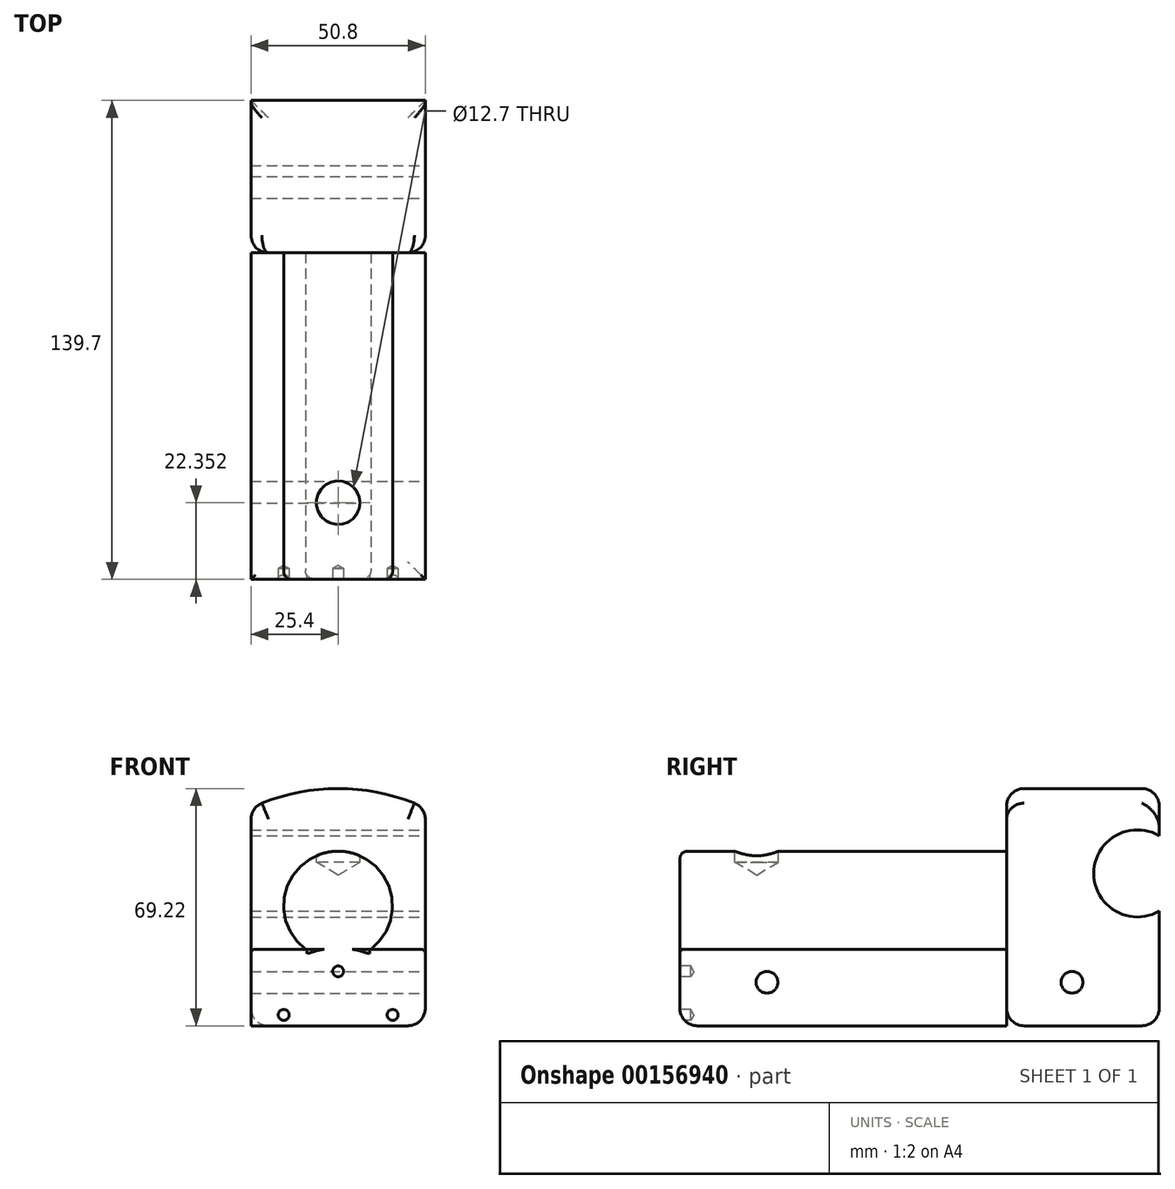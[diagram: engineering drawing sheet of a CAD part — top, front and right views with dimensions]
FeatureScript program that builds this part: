
annotation { "Feature Type Name" : "Feature", "Feature Type Description" : "" }
export const myFeature = defineFeature(function(context is Context, id is Id, definition is map)
    precondition{}
    {
        {
            var Q0;
            Q0=qCreatedBy(makeId("Front.planeOp"),FACE);
            var sketch = newSketch(context, id + "F0", { "sketchPlane" : qUnion([Q0])});
            skLineSegment(sketch, "E0.bottom", {"start": v(25.4, -11.18) * mm, "end": v(-25.4, -11.18) * mm});
            skLineSegment(sketch, "E0.top", {"start": v(25.4, 11.18) * mm, "end": v(-25.4, 11.18) * mm});
            skLineSegment(sketch, "E0.left", {"start": v(25.4, -11.18) * mm, "end": v(25.4, 11.18) * mm});
            skLineSegment(sketch, "E0.right", {"start": v(-25.4, -11.18) * mm, "end": v(-25.4, 11.18) * mm});
            skPoint(sketch, "E0.middle", {"position": v(0, 0) * mm});
            skCircle(sketch, "E1", {"center": v(0, 23.88) * mm, "radius": 15.88 * mm});
            skLineSegment(sketch, "E2.bottom", {"start": v(-25.4, -11.18) * mm, "end": v(-15.88, -11.18) * mm});
            skLineSegment(sketch, "E2.left", {"start": v(-25.4, -11.18) * mm, "end": v(-25.4, -8) * mm});
            skPoint(sketch, "E3", {"position": v(-15.88, -8) * mm});
            skLineSegment(sketch, "E4", {"start": v(0, 0) * mm, "end": v(0, -11.18) * mm});
            skPoint(sketch, "E5", {"position": v(15.88, -8) * mm});
            skPoint(sketch, "E6.MirrorCS.start.orphan", {"position": v(25.4, -8) * mm});
            skLineSegment(sketch, "E7.bottom", {"start": v(-25.4, -11.18) * mm, "end": v(0, -11.18) * mm});
            skLineSegment(sketch, "E7.top", {"start": v(-25.4, 4.7) * mm, "end": v(0, 4.7) * mm});
            skLineSegment(sketch, "E7.left", {"start": v(-25.4, -11.18) * mm, "end": v(-25.4, 4.7) * mm});
            skLineSegment(sketch, "E7.right", {"start": v(0, -11.18) * mm, "end": v(0, 4.7) * mm});
            skPoint(sketch, "E8", {"position": v(0, 4.7) * mm});
            skSolve(sketch);
        }
        {
            var Q0;
            Q0 = qSketchRegion(id + "F0", true);
            extrude(context, id + "F1", {"entities" : qUnion([Q0]), "oppositeDirection" : true, "depth" : 95.25 * mm});
        }
        {
            var Q0;
            Q0=sQuery(id+"F0.wireOp",VERTEX,"E8");
            var Q1;
            Q1=sQuery(id+"F0.wireOp",VERTEX,"E5");
            var Q2;
            Q2=sQuery(id+"F0.wireOp",VERTEX,"E3");
            var Q3;
            Q3=makeQuery(id+"F1.opExtrude","SWEPT_BODY",BODY,{"disambiguationData":[OSD([sQuery(id+"F0.wireOp",EDGE,"E0.bottom"),sQuery(id+"F0.wireOp",EDGE,"E0.top"),sQuery(id+"F0.wireOp",EDGE,"E0.left"),sQuery(id+"F0.wireOp",EDGE,"E0.right"),sQuery(id+"F0.wireOp",EDGE,"E1"),sQuery(id+"F0.wireOp",EDGE,"E7.bottom"),sQuery(id+"F0.wireOp",EDGE,"E7.left")])]});
            hole(context, id + "F2", {"style" : HoleStyle.SIMPLE, "endStyle" : HoleEndStyle.BLIND, "holeDiameter" : 3.17 * mm, "holeDepth" : 3.17 * mm, "startFromSketch" : true, "locations" : qUnion([Q0, Q1, Q2]), "scope" : qUnion([Q3])});
        }
        {
            var Q0;
            Q0=makeQuery(id+"F1.opExtrude","SWEPT_FACE",FACE,{"disambiguationData":[OSD([sQuery(id+"F0.wireOp",EDGE,"E0.bottom"),sQuery(id+"F0.wireOp",EDGE,"E7.bottom")])]});
            cPlane(context, id + "F3", {"entities" : qUnion([Q0]), "cplaneType" : CPlaneType.OFFSET, "offset" : 54.1 * mm, "oppositeDirection" : true, "width" : 152.4 * mm, "height" : 152.4 * mm});
        }
        {
            var Q0;
            Q0=qCreatedBy(id+"F3.planeOp",FACE);
            var sketch = newSketch(context, id + "F4", { "sketchPlane" : qUnion([Q0])});
            skLineSegment(sketch, "E9.0", {"start": v(-15.88, 0) * mm, "end": v(15.88, 0) * mm});
            skLineSegment(sketch, "E10", {"start": v(0, 0) * mm, "end": v(0, -22.35) * mm});
            skPoint(sketch, "E11", {"position": v(0, -22.35) * mm});
            skSolve(sketch);
        }
        {
            var Q0;
            Q0=sQuery(id+"F4.wireOp",VERTEX,"E11");
            var Q1;
            Q1=makeQuery(id+"F1.opExtrude","SWEPT_BODY",BODY,{"disambiguationData":[OSD([sQuery(id+"F0.wireOp",EDGE,"E0.bottom"),sQuery(id+"F0.wireOp",EDGE,"E0.top"),sQuery(id+"F0.wireOp",EDGE,"E0.left"),sQuery(id+"F0.wireOp",EDGE,"E0.right"),sQuery(id+"F0.wireOp",EDGE,"E1"),sQuery(id+"F0.wireOp",EDGE,"E7.bottom"),sQuery(id+"F0.wireOp",EDGE,"E7.left")])]});
            hole(context, id + "F5", {"style" : HoleStyle.SIMPLE, "endStyle" : HoleEndStyle.BLIND, "oppositeDirection" : true, "holeDiameter" : 12.7 * mm, "holeDepth" : 6.35 * mm, "startFromSketch" : true, "locations" : qUnion([Q0]), "scope" : qUnion([Q1])});
        }
        {
            var Q0;
            Q0=makeQuery(id+"F1.opExtrude","CAP_FACE",FACE,{"disambiguationData":[OSD([sQuery(id+"F0.wireOp",EDGE,"E0.bottom"),sQuery(id+"F0.wireOp",EDGE,"E0.top"),sQuery(id+"F0.wireOp",EDGE,"E0.left"),sQuery(id+"F0.wireOp",EDGE,"E0.right"),sQuery(id+"F0.wireOp",EDGE,"E1"),sQuery(id+"F0.wireOp",EDGE,"E7.bottom"),sQuery(id+"F0.wireOp",EDGE,"E7.left")])],"isStart":false});
            var sketch = newSketch(context, id + "F6", { "sketchPlane" : qUnion([Q0])});
            skLineSegment(sketch, "E12", {"start": v(-25.4, -11.18) * mm, "end": v(-25.4, -1.65) * mm});
            skLineSegment(sketch, "E13", {"start": v(-25.4, -1.65) * mm, "end": v(0, -1.65) * mm});
            skPoint(sketch, "E14", {"position": v(0, -1.65) * mm});
            skArc(sketch, "E15", {"start": v(25.4, 52.37) * mm, "mid": v(0, 58.04) * mm, "end": v(-25.4, 52.37) * mm});
            skLineSegment(sketch, "E16", {"start": v(-25.4, 11.18) * mm, "end": v(-25.4, 52.37) * mm});
            skLineSegment(sketch, "E17", {"start": v(25.4, 11.18) * mm, "end": v(25.4, 52.37) * mm});
            skSolve(sketch);
        }
        {
            var Q0;
            Q0 = qSketchRegion(id + "F6", true);
            var Q1;
            Q1=makeQuery(id+"F6.imprint","IMPRINT",FACE,{"disambiguationData":[TD([[makeQuery(id+"F6.imprint","IMPRINT",EDGE,{"derivedFrom":sQuery(id+"F6.wireOp",EDGE,"E15")}),1.0]])]});
            var Q2;
            {var subQ5=sQuery(id+"F6.wireOp",EDGE,"E12");Q2=makeQuery(id+"F6.imprint","IMPRINT",FACE,{"disambiguationData":[TD([[makeQuery(id+"F6.imprint","IMPRINT",EDGE,{"derivedFrom":subQ5}),-1.0]])]});}
            extrude(context, id + "F7", {"entities" : qUnion([Q0, Q1, Q2]), "depth" : 44.45 * mm});
        }
        {
            var Q0;
            Q0=makeQuery(id+"F7.opExtrude","SWEPT_FACE",FACE,{"disambiguationData":[OSD([sQuery(id+"F0.wireOp",EDGE,"E0.left"),sQuery(id+"F6.wireOp",EDGE,"E12"),sQuery(id+"F6.wireOp",EDGE,"E16")])]});
            var sketch = newSketch(context, id + "F8", { "sketchPlane" : qUnion([Q0])});
            skLineSegment(sketch, "E18.bottom", {"start": v(139.7, -11.18) * mm, "end": v(133.35, -11.18) * mm});
            skLineSegment(sketch, "E18.top", {"start": v(139.7, 33.27) * mm, "end": v(133.35, 33.27) * mm});
            skLineSegment(sketch, "E18.left", {"start": v(139.7, -11.18) * mm, "end": v(139.7, 33.27) * mm});
            skLineSegment(sketch, "E18.right", {"start": v(133.35, -11.18) * mm, "end": v(133.35, 33.27) * mm});
            skPoint(sketch, "E19", {"position": v(133.35, 33.27) * mm});
            skLineSegment(sketch, "E20.bottom", {"start": v(139.7, -11.18) * mm, "end": v(114.3, -11.18) * mm});
            skLineSegment(sketch, "E20.top", {"start": v(139.7, 1.52) * mm, "end": v(114.3, 1.52) * mm});
            skLineSegment(sketch, "E20.left", {"start": v(139.7, -11.18) * mm, "end": v(139.7, 1.52) * mm});
            skLineSegment(sketch, "E20.right", {"start": v(114.3, -11.18) * mm, "end": v(114.3, 1.52) * mm});
            skPoint(sketch, "E21", {"position": v(114.3, 1.52) * mm});
            skLineSegment(sketch, "E22.bottom", {"start": v(139.7, -11.18) * mm, "end": v(25.4, -11.18) * mm});
            skLineSegment(sketch, "E22.top", {"start": v(139.7, 1.52) * mm, "end": v(25.4, 1.52) * mm});
            skLineSegment(sketch, "E22.right", {"start": v(25.4, -11.18) * mm, "end": v(25.4, 1.52) * mm});
            skPoint(sketch, "E23", {"position": v(25.4, 1.52) * mm});
            skSolve(sketch);
        }
        {
            var Q0;
            Q0=sQuery(id+"F8.wireOp",VERTEX,"E23");
            var Q1;
            Q1=sQuery(id+"F8.wireOp",VERTEX,"E21");
            var Q2;
            Q2=makeQuery(id+"F7.opExtrude","SWEPT_BODY",BODY,{"disambiguationData":[OSD([sQuery(id+"F0.wireOp",EDGE,"E0.bottom"),sQuery(id+"F0.wireOp",EDGE,"E0.left"),sQuery(id+"F0.wireOp",EDGE,"E0.right"),sQuery(id+"F0.wireOp",EDGE,"E7.bottom"),sQuery(id+"F0.wireOp",EDGE,"E7.left"),sQuery(id+"F6.wireOp",EDGE,"E12"),sQuery(id+"F6.wireOp",EDGE,"E15"),sQuery(id+"F6.wireOp",EDGE,"E16"),sQuery(id+"F6.wireOp",EDGE,"E17")])]});
            var Q3;
            Q3=makeQuery(id+"F1.opExtrude","SWEPT_BODY",BODY,{"disambiguationData":[OSD([sQuery(id+"F0.wireOp",EDGE,"E0.bottom"),sQuery(id+"F0.wireOp",EDGE,"E0.top"),sQuery(id+"F0.wireOp",EDGE,"E0.left"),sQuery(id+"F0.wireOp",EDGE,"E0.right"),sQuery(id+"F0.wireOp",EDGE,"E1"),sQuery(id+"F0.wireOp",EDGE,"E7.bottom"),sQuery(id+"F0.wireOp",EDGE,"E7.left")])]});
            hole(context, id + "F9", {"style" : HoleStyle.SIMPLE, "endStyle" : HoleEndStyle.THROUGH, "holeDiameter" : 6.35 * mm, "startFromSketch" : true, "locations" : qUnion([Q0, Q1]), "scope" : qUnion([Q2, Q3]), "isTappedThrough" : true});
        }
        {
            var Q0;
            Q0=sQuery(id+"F8.wireOp",VERTEX,"E19");
            var Q1;
            Q1=makeQuery(id+"F7.opExtrude","SWEPT_BODY",BODY,{"disambiguationData":[OSD([sQuery(id+"F0.wireOp",EDGE,"E0.bottom"),sQuery(id+"F0.wireOp",EDGE,"E0.left"),sQuery(id+"F0.wireOp",EDGE,"E0.right"),sQuery(id+"F0.wireOp",EDGE,"E7.bottom"),sQuery(id+"F0.wireOp",EDGE,"E7.left"),sQuery(id+"F6.wireOp",EDGE,"E12"),sQuery(id+"F6.wireOp",EDGE,"E15"),sQuery(id+"F6.wireOp",EDGE,"E16"),sQuery(id+"F6.wireOp",EDGE,"E17")])]});
            hole(context, id + "F10", {"style" : HoleStyle.SIMPLE, "endStyle" : HoleEndStyle.THROUGH, "holeDiameter" : 25.4 * mm, "startFromSketch" : true, "locations" : qUnion([Q0]), "scope" : qUnion([Q1]), "isTappedThrough" : true});
        }
        {
            var Q0;
            Q0=makeQuery(id+"F7.opExtrude","CAP_EDGE",EDGE,{"disambiguationData":[OSD([sQuery(id+"F6.wireOp",EDGE,"E15")])],"isStart":true});
            var Q1;
            Q1=makeQuery(id+"F7.opExtrude","SWEPT_EDGE",EDGE,{"disambiguationData":[OSD([sQuery(id+"F6.wireOp",EDGE,"E15"),sQuery(id+"F6.wireOp",EDGE,"E17")])]});
            var Q2;
            Q2=makeQuery(id+"F7.opExtrude","CAP_EDGE",EDGE,{"disambiguationData":[OSD([sQuery(id+"F6.wireOp",EDGE,"E15")])],"isStart":false});
            var Q3;
            Q3=makeQuery(id+"F7.opExtrude","SWEPT_EDGE",EDGE,{"disambiguationData":[OSD([sQuery(id+"F6.wireOp",EDGE,"E15"),sQuery(id+"F6.wireOp",EDGE,"E16")])]});
            var Q4;
            Q4=makeQuery(id+"F7.opExtrude","CAP_EDGE",EDGE,{"disambiguationData":[OSD([sQuery(id+"F0.wireOp",EDGE,"E0.bottom"),sQuery(id+"F0.wireOp",EDGE,"E7.bottom")])],"isStart":false});
            var Q5;
            Q5=makeQuery(id+"F7.opExtrude","SWEPT_EDGE",EDGE,{"disambiguationData":[OSD([sQuery(id+"F0.wireOp",EDGE,"E0.bottom"),sQuery(id+"F0.wireOp",EDGE,"E7.bottom"),sQuery(id+"F6.wireOp",EDGE,"E12")])]});
            var Q6;
            Q6=makeQuery(id+"F1.opExtrude","SWEPT_EDGE",EDGE,{"disambiguationData":[OSD([sQuery(id+"F0.wireOp",EDGE,"E0.bottom"),sQuery(id+"F0.wireOp",EDGE,"E0.left")])]});
            var Q7;
            Q7=makeQuery(id+"F7.opExtrude","SWEPT_EDGE",EDGE,{"disambiguationData":[OSD([sQuery(id+"F0.wireOp",EDGE,"E0.bottom"),sQuery(id+"F0.wireOp",EDGE,"E0.right"),sQuery(id+"F0.wireOp",EDGE,"E7.bottom"),sQuery(id+"F0.wireOp",EDGE,"E7.left")])]});
            var Q8;
            Q8=makeQuery(id+"F1.opExtrude","SWEPT_EDGE",EDGE,{"disambiguationData":[OSD([sQuery(id+"F0.wireOp",EDGE,"E7.bottom"),sQuery(id+"F0.wireOp",EDGE,"E7.left")])]});
            var Q9;
            Q9=makeQuery(id+"F1.opExtrude","CAP_EDGE",EDGE,{"disambiguationData":[OSD([sQuery(id+"F0.wireOp",EDGE,"E0.bottom"),sQuery(id+"F0.wireOp",EDGE,"E7.bottom")])],"isStart":true});
            fillet(context, id + "F11", {"entities" : qUnion([Q0, Q1, Q2, Q3, Q4, Q5, Q6, Q7, Q8, Q9]), "radius" : 5.08 * mm, "tangentPropagation" : true, "allowEdgeOverflow" : false});
        }
        {
            var Q0;
            Q0=makeQuery(id+"F1.opExtrude","CAP_EDGE",EDGE,{"disambiguationData":[OSD([sQuery(id+"F0.wireOp",EDGE,"E1")])],"isStart":true});
            fillet(context, id + "F12", {"entities" : qUnion([Q0]), "radius" : 2.54 * mm, "rho" : 0.5, "crossSection" : FilletCrossSection.CONIC, "allowEdgeOverflow" : false});
        }
        {
            var Q0;
            Q0=makeQuery(id+"F1.opExtrude","SWEPT_EDGE",EDGE,{"disambiguationData":[OSD([sQuery(id+"F0.wireOp",EDGE,"E0.top"),sQuery(id+"F0.wireOp",EDGE,"E0.left")])]});
            var Q1;
            {var subQ0=sQuery(id+"F0.wireOp",EDGE,"E0.top");Q1=makeQuery(id+"F1.opExtrude","CAP_EDGE",EDGE,{"disambiguationData":[OSD([subQ0]),TDD([makeQuery(id+"F0.imprint","IMPRINT",EDGE,{"disambiguationData":[TD([[makeQuery(id+"F0.imprint","INTERSECT",VERTEX,{"derivedFrom":[subQ0,sQuery(id+"F0.wireOp",EDGE,"E0.left")]}),-1.0]])],"derivedFrom":subQ0})])],"isStart":true});}
            var Q2;
            {var subQ0=sQuery(id+"F0.wireOp",EDGE,"E0.top");Q2=makeQuery(id+"F1.opExtrude","CAP_EDGE",EDGE,{"disambiguationData":[OSD([subQ0]),TDD([makeQuery(id+"F0.imprint","IMPRINT",EDGE,{"disambiguationData":[TD([[makeQuery(id+"F0.imprint","INTERSECT",VERTEX,{"derivedFrom":[subQ0,sQuery(id+"F0.wireOp",EDGE,"E0.right")]}),1.0]])],"derivedFrom":subQ0})])],"isStart":true});}
            var Q3;
            Q3=makeQuery(id+"F1.opExtrude","SWEPT_EDGE",EDGE,{"disambiguationData":[OSD([sQuery(id+"F0.wireOp",EDGE,"E0.top"),sQuery(id+"F0.wireOp",EDGE,"E0.right")])]});
            fillet(context, id + "F13", {"entities" : qUnion([Q0, Q1, Q2, Q3]), "radius" : 1.27 * mm, "tangentPropagation" : true, "allowEdgeOverflow" : false});
        }
        {
            var Q0;
            Q0=makeQuery(id+"F7.opExtrude","CAP_EDGE",EDGE,{"disambiguationData":[OSD([sQuery(id+"F0.wireOp",EDGE,"E0.right"),sQuery(id+"F0.wireOp",EDGE,"E7.left"),sQuery(id+"F6.wireOp",EDGE,"E17")])],"isStart":true});
            var Q1;
            Q1=makeQuery(id+"F7.opExtrude","CAP_EDGE",EDGE,{"disambiguationData":[OSD([sQuery(id+"F0.wireOp",EDGE,"E0.left"),sQuery(id+"F6.wireOp",EDGE,"E12"),sQuery(id+"F6.wireOp",EDGE,"E16")])],"isStart":true});
            var Q2;
            Q2=makeQuery(id+"F10.hole-0.boolean.opBoolean","INTERSECT",EDGE,{"disambiguationData":[OD(1.0)],"derivedFrom":[makeQuery(id+"F7.opExtrude","CAP_FACE",FACE,{"disambiguationData":[OSD([sQuery(id+"F0.wireOp",EDGE,"E0.bottom"),sQuery(id+"F0.wireOp",EDGE,"E0.left"),sQuery(id+"F0.wireOp",EDGE,"E0.right"),sQuery(id+"F0.wireOp",EDGE,"E7.bottom"),sQuery(id+"F0.wireOp",EDGE,"E7.left"),sQuery(id+"F6.wireOp",EDGE,"E12"),sQuery(id+"F6.wireOp",EDGE,"E15"),sQuery(id+"F6.wireOp",EDGE,"E16"),sQuery(id+"F6.wireOp",EDGE,"E17")])],"isStart":false}),makeQuery(id+"F10.hole-0.opRevolve","SWEPT_FACE",FACE,{"disambiguationData":[OSD([sQuery(id+"F10.hole-0.sketch.wireOp",EDGE,"core_line_2")])]})]});
            var Q3;
            Q3=makeQuery(id+"F10.hole-0.boolean.opBoolean","COPY",EDGE,{"derivedFrom":makeQuery(id+"F10.hole-0.opRevolve","SWEPT_EDGE",EDGE,{"disambiguationData":[OSD([sQuery(id+"F10.hole-0.sketch.wireOp",EDGE,"core_line_2"),sQuery(id+"F10.hole-0.sketch.wireOp",EDGE,"core_line_3")])]})});
            var Q4;
            Q4=makeQuery(id+"F10.hole-0.boolean.opBoolean","INTERSECT",EDGE,{"derivedFrom":[makeQuery(id+"F7.opExtrude","SWEPT_FACE",FACE,{"disambiguationData":[OSD([sQuery(id+"F0.wireOp",EDGE,"E0.right"),sQuery(id+"F0.wireOp",EDGE,"E7.left"),sQuery(id+"F6.wireOp",EDGE,"E17")])]}),makeQuery(id+"F10.hole-0.opRevolve","SWEPT_FACE",FACE,{"disambiguationData":[OSD([sQuery(id+"F10.hole-0.sketch.wireOp",EDGE,"core_line_2")])]})]});
            fillet(context, id + "F14", {"entities" : qUnion([Q0, Q1, Q2, Q3, Q4]), "radius" : 5.08 * mm, "tangentPropagation" : true, "allowEdgeOverflow" : false});
        }
    });
